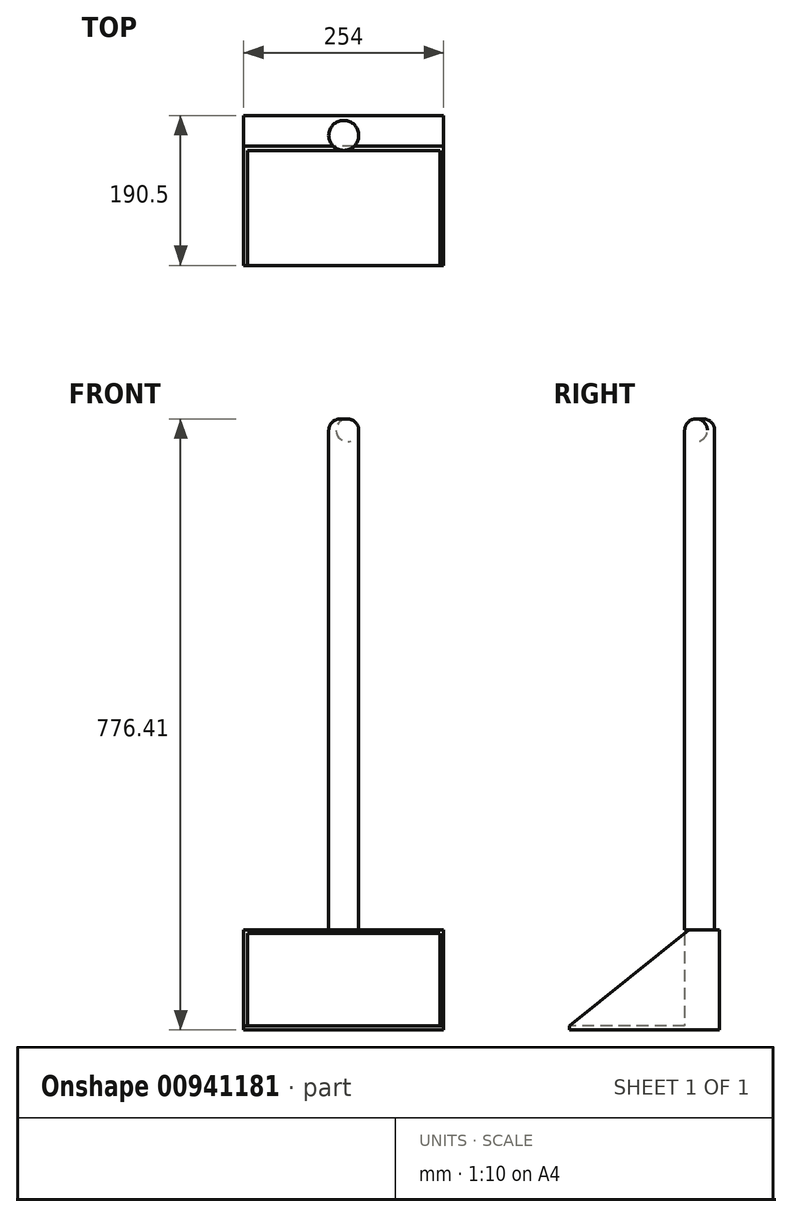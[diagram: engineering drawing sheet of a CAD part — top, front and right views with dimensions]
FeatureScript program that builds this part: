
annotation { "Feature Type Name" : "Feature", "Feature Type Description" : "" }
export const myFeature = defineFeature(function(context is Context, id is Id, definition is map)
    precondition{}
    {
        {
            var Q0;
            Q0=qCreatedBy(makeId("Front.planeOp"),FACE);
            var sketch = newSketch(context, id + "F0", { "sketchPlane" : qUnion([Q0])});
            skLineSegment(sketch, "E0.top", {"start": v(-19.05, 0) * mm, "end": v(0, 0) * mm});
            skLineSegment(sketch, "E0.left", {"start": v(-19.05, 762) * mm, "end": v(-19.05, 0) * mm});
            skLineSegment(sketch, "E0.right", {"start": v(0, 762) * mm, "end": v(0, 0) * mm});
            skLineSegment(sketch, "E1", {"start": v(0, 762) * mm, "end": v(0, 775.65) * mm});
            skArc(sketch, "E2", {"start": v(0, 775.65) * mm, "mid": v(-13.03, 773.72) * mm, "end": v(-19.05, 762) * mm});
            skSolve(sketch);
        }
        {
            var Q0;
            Q0 = qSketchRegion(id + "F0", true);
            var Q1;
            Q1=sQuery(id+"F0.wireOp",EDGE,"E0.right");
            revolve(context, id + "F1", {"surfaceOperationType" : NewSurfaceOperationType.NEW, "entities" : qUnion([Q0]), "axis" : qUnion([Q1]), "revolveType" : RevolveType.FULL});
        }
        {
            var Q0;
            Q0=qCreatedBy(makeId("Front.planeOp"),FACE);
            var sketch = newSketch(context, id + "F2", { "sketchPlane" : qUnion([Q0])});
            skLineSegment(sketch, "E3.bottom", {"start": v(-127, 127) * mm, "end": v(127, 127) * mm});
            skLineSegment(sketch, "E3.top", {"start": v(-127, 0) * mm, "end": v(127, 0) * mm});
            skLineSegment(sketch, "E3.left", {"start": v(-127, 127) * mm, "end": v(-127, 0) * mm});
            skLineSegment(sketch, "E3.right", {"start": v(127, 127) * mm, "end": v(127, 0) * mm});
            skLineSegment(sketch, "E4", {"start": v(0, 0) * mm, "end": v(0, 136.62) * mm, "construction": true});
            skSolve(sketch);
        }
        {
            var Q0;
            Q0 = qSketchRegion(id + "F2", true);
            extrude(context, id + "F3", {"entities" : qUnion([Q0]), "operationType" : NewBodyOperationType.ADD, "depth" : 165.1 * mm, "offsetDistance" : 25.4 * mm, "hasSecondDirection" : true, "secondDirectionOppositeDirection" : true, "secondDirectionDepth" : 25.4 * mm});
        }
        {
            var Q0;
            Q0=makeQuery(id+"F3.opExtrude","SWEPT_FACE",FACE,{"disambiguationData":[OSD([sQuery(id+"F2.wireOp",EDGE,"E3.left")])]});
            var sketch = newSketch(context, id + "F4", { "sketchPlane" : qUnion([Q0])});
            skLineSegment(sketch, "E5", {"start": v(13.76, 127) * mm, "end": v(165.1, 127) * mm});
            skLineSegment(sketch, "E6", {"start": v(165.1, 127) * mm, "end": v(165.1, 5.08) * mm});
            skLineSegment(sketch, "E7", {"start": v(13.76, 127) * mm, "end": v(165.1, 5.08) * mm});
            skSolve(sketch);
        }
        {
            var Q0;
            Q0 = qSketchRegion(id + "F4", true);
            extrude(context, id + "F5", {"entities" : qUnion([Q0]), "operationType" : NewBodyOperationType.REMOVE, "oppositeDirection" : true, "depth" : 386.08 * mm, "offsetDistance" : 25.4 * mm});
        }
        {
            var Q0;
            Q0=makeQuery(id+"F3.opExtrude","CAP_FACE",FACE,{"disambiguationData":[OSD([sQuery(id+"F2.wireOp",EDGE,"E3.bottom"),sQuery(id+"F2.wireOp",EDGE,"E3.top"),sQuery(id+"F2.wireOp",EDGE,"E3.left"),sQuery(id+"F2.wireOp",EDGE,"E3.right")])],"isStart":false});
            var sketch = newSketch(context, id + "F6", { "sketchPlane" : qUnion([Q0])});
            skLineSegment(sketch, "E8.bottom", {"start": v(-121.99, 124.68) * mm, "end": v(122.4, 124.68) * mm});
            skLineSegment(sketch, "E8.top", {"start": v(-121.99, 5.08) * mm, "end": v(122.4, 5.08) * mm});
            skLineSegment(sketch, "E8.left", {"start": v(-121.99, 124.68) * mm, "end": v(-121.99, 5.08) * mm});
            skLineSegment(sketch, "E8.right", {"start": v(122.4, 124.68) * mm, "end": v(122.4, 5.08) * mm});
            skSolve(sketch);
        }
        {
            var Q0;
            Q0 = qSketchRegion(id + "F6", true);
            extrude(context, id + "F7", {"entities" : qUnion([Q0]), "operationType" : NewBodyOperationType.REMOVE, "oppositeDirection" : true, "depth" : 146.05 * mm, "offsetDistance" : 25.4 * mm});
        }
    });
